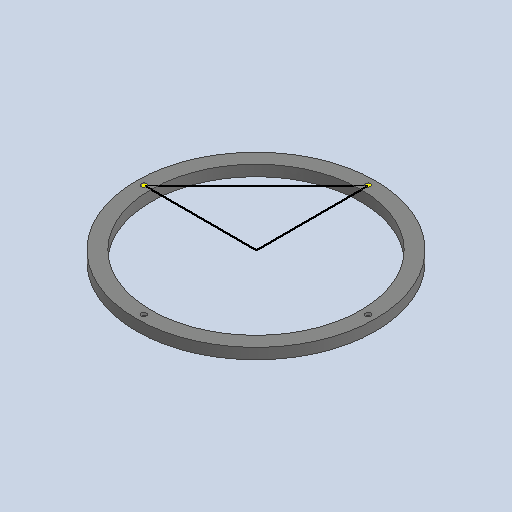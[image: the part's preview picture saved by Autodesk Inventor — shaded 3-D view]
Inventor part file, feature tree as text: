
AUTODESK INVENTOR PART (.ipt)
format: ipt  version: 2023 (Build 270158000, 158)  size: 274,944 bytes
history: native  units: in
note: dims shown in document units (in); Inventor stores cm internally (conversion verified against a paired STEP export)
features: sketch x3, extrude x1, hole x1, pattern_circular x1
ambient origin geometry x8: Origin, YZ Plane, XZ Plane, XY Plane, X Axis, Y Axis, Z Axis, Center Point
bodies: Solid1 (feature_tree)
feature tree (6):
  extrude  "Extrusion1"  Depth=8.7598in
  hole  "Hole1"  [1 undecoded]
  pattern_circular  "Circular Pattern1"  Count=4 Angle=360.0deg
  sketch  "Sketch3"  dims[d5=0.0984in d6=0.2362in d7=0.1969in d8=0.0787in d9=90.0deg d10=0.315in d11=0.8108in d12=1.5748in d13=360.0deg]
  sketch  "Sketch1"  dims[d0=7.6772in d1=8.7598in]
  sketch  "Sketch2"  dims[d2=0.3937in d3=0.0in d4=4.1093in]
note: 1 required parameter value undecoded (feature->parameter linkage not recoverable at this tier; creation-order binding heuristic only, values carry confidence <= 0.55)
